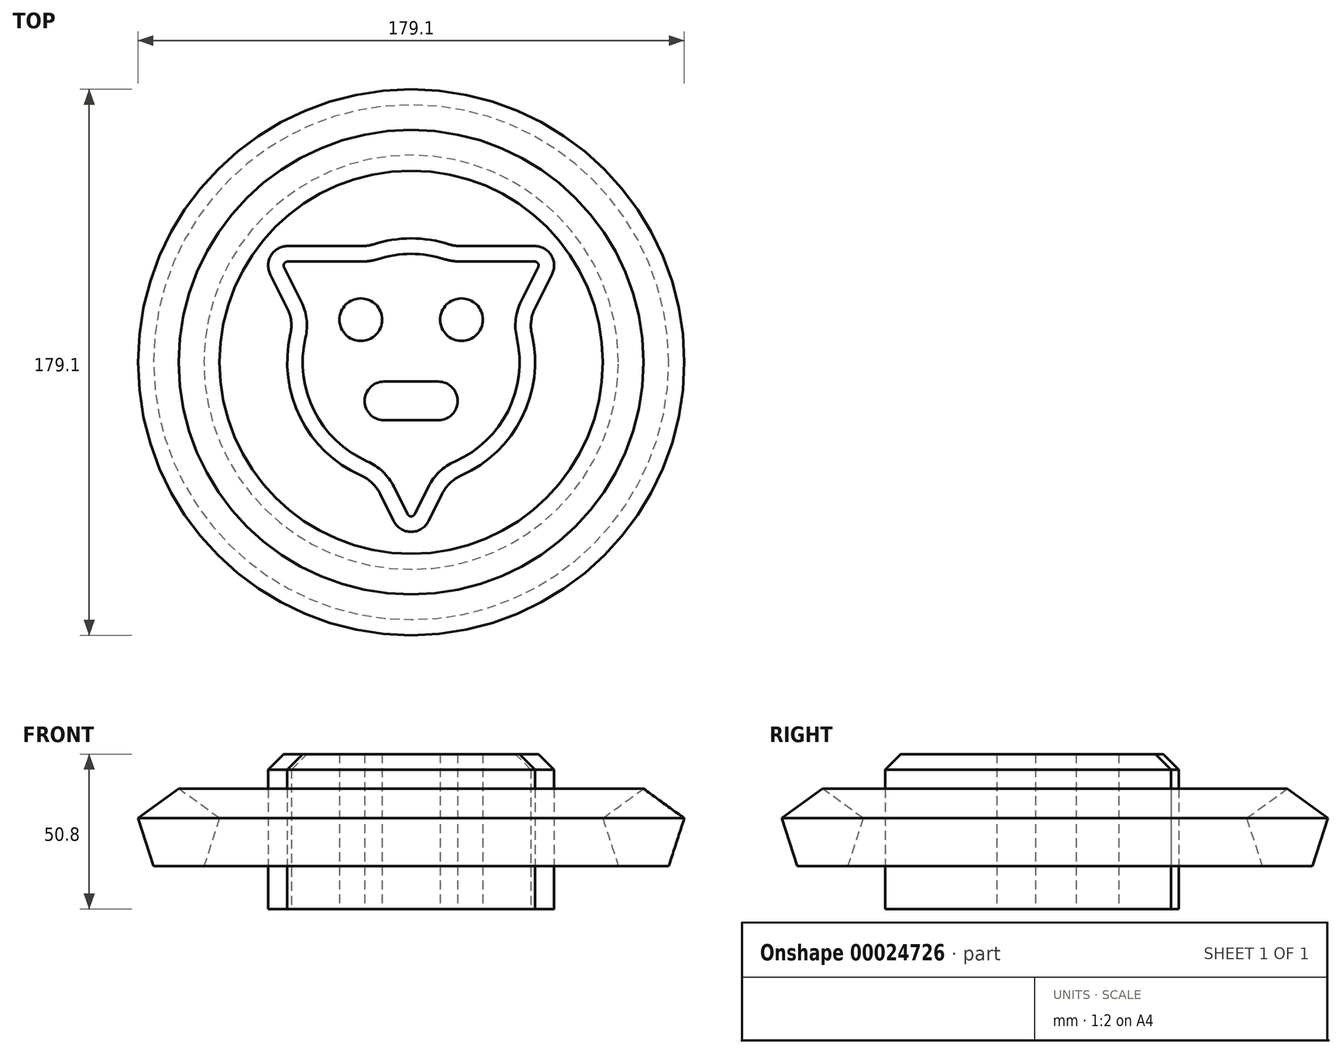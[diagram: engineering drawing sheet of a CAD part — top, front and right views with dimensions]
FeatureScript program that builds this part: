
annotation { "Feature Type Name" : "Feature", "Feature Type Description" : "" }
export const myFeature = defineFeature(function(context is Context, id is Id, definition is map)
    precondition{}
    {
        {
            var Q0;
            Q0=qCreatedBy(makeId("Top.planeOp"),FACE);
            var sketch = newSketch(context, id + "F0", { "sketchPlane" : qUnion([Q0])});
            skArc(sketch, "E0", {"start": v(-38.4, 13.3) * mm, "mid": v(-36.35, -18.17) * mm, "end": v(-12.4, -38.7) * mm});
            skLineSegment(sketch, "E1", {"start": v(-50.8, 38.1) * mm, "end": v(-14.14, 38.1) * mm});
            skLineSegment(sketch, "E2", {"start": v(50.8, 38.1) * mm, "end": v(38.4, 13.3) * mm});
            skLineSegment(sketch, "E3", {"start": v(0, -63.5) * mm, "end": v(-12.4, -38.7) * mm});
            skArc(sketch, "E4.trimOffspring", {"start": v(14.14, 38.1) * mm, "mid": v(0, 40.64) * mm, "end": v(-14.14, 38.1) * mm});
            skArc(sketch, "E5.trimOffspring", {"start": v(12.4, -38.7) * mm, "mid": v(36.35, -18.17) * mm, "end": v(38.4, 13.3) * mm});
            skLineSegment(sketch, "E6.trimOffspring", {"start": v(12.4, -38.7) * mm, "end": v(0, -63.5) * mm});
            skLineSegment(sketch, "E7.trimOffspring", {"start": v(-38.4, 13.3) * mm, "end": v(-50.8, 38.1) * mm});
            skLineSegment(sketch, "E8.trimOffspring", {"start": v(14.14, 38.1) * mm, "end": v(50.8, 38.1) * mm});
            skSolve(sketch);
        }
        {
            var Q0;
            Q0=makeQuery(id+"F0.imprint","IMPRINT",FACE,{"disambiguationData":[TD([[makeQuery(id+"F0.imprint","IMPRINT",EDGE,{"derivedFrom":sQuery(id+"F0.wireOp",EDGE,"E0")}),1.0]])]});
            extrude(context, id + "F1", {"entities" : qUnion([Q0]), "depth" : 50.8 * mm});
        }
        {
            var Q0;
            Q0=makeQuery(id+"F1.opExtrude","SWEPT_EDGE",EDGE,{"disambiguationData":[OSD([sQuery(id+"F0.wireOp",EDGE,"E5.trimOffspring"),sQuery(id+"F0.wireOp",EDGE,"E6.trimOffspring")])]});
            var Q1;
            Q1=makeQuery(id+"F1.opExtrude","SWEPT_EDGE",EDGE,{"disambiguationData":[OSD([sQuery(id+"F0.wireOp",EDGE,"E0"),sQuery(id+"F0.wireOp",EDGE,"E3")])]});
            var Q2;
            Q2=makeQuery(id+"F1.opExtrude","SWEPT_EDGE",EDGE,{"disambiguationData":[OSD([sQuery(id+"F0.wireOp",EDGE,"E0"),sQuery(id+"F0.wireOp",EDGE,"E7.trimOffspring")])]});
            var Q3;
            Q3=makeQuery(id+"F1.opExtrude","SWEPT_EDGE",EDGE,{"disambiguationData":[OSD([sQuery(id+"F0.wireOp",EDGE,"E1"),sQuery(id+"F0.wireOp",EDGE,"E4.trimOffspring")])]});
            var Q4;
            Q4=makeQuery(id+"F1.opExtrude","SWEPT_EDGE",EDGE,{"disambiguationData":[OSD([sQuery(id+"F0.wireOp",EDGE,"E4.trimOffspring"),sQuery(id+"F0.wireOp",EDGE,"E8.trimOffspring")])]});
            var Q5;
            Q5=makeQuery(id+"F1.opExtrude","SWEPT_EDGE",EDGE,{"disambiguationData":[OSD([sQuery(id+"F0.wireOp",EDGE,"E2"),sQuery(id+"F0.wireOp",EDGE,"E5.trimOffspring")])]});
            fillet(context, id + "F2", {"entities" : qUnion([Q0, Q1, Q2, Q3, Q4, Q5]), "radius" : 12.7 * mm, "tangentPropagation" : true, "allowEdgeOverflow" : false});
        }
        {
            var Q0;
            Q0=makeQuery(id+"F1.opExtrude","SWEPT_EDGE",EDGE,{"disambiguationData":[OSD([sQuery(id+"F0.wireOp",EDGE,"E3"),sQuery(id+"F0.wireOp",EDGE,"E6.trimOffspring")])]});
            var Q1;
            Q1=makeQuery(id+"F1.opExtrude","SWEPT_EDGE",EDGE,{"disambiguationData":[OSD([sQuery(id+"F0.wireOp",EDGE,"E2"),sQuery(id+"F0.wireOp",EDGE,"E8.trimOffspring")])]});
            var Q2;
            Q2=makeQuery(id+"F1.opExtrude","SWEPT_EDGE",EDGE,{"disambiguationData":[OSD([sQuery(id+"F0.wireOp",EDGE,"E1"),sQuery(id+"F0.wireOp",EDGE,"E7.trimOffspring")])]});
            fillet(context, id + "F3", {"entities" : qUnion([Q0, Q1, Q2]), "radius" : 6.35 * mm, "tangentPropagation" : true, "allowEdgeOverflow" : false});
        }
        {
            var Q0;
            Q0=makeQuery(id+"F1.opExtrude","CAP_EDGE",EDGE,{"disambiguationData":[OSD([sQuery(id+"F0.wireOp",EDGE,"E0")])],"isStart":false});
            chamfer(context, id + "F4", {"entities" : qUnion([Q0]), "width" : 5.08 * mm, "tangentPropagation" : true});
        }
        {
            var Q0;
            Q0=qCreatedBy(makeId("Top.planeOp"),FACE);
            var sketch = newSketch(context, id + "F5", { "sketchPlane" : qUnion([Q0])});
            skCircle(sketch, "E9", {"center": v(-16.51, 13.97) * mm, "radius": 6.99 * mm});
            skCircle(sketch, "E10", {"center": v(16.51, 13.97) * mm, "radius": 6.99 * mm});
            skArc(sketch, "E11", {"start": v(-8.9, -6.35) * mm, "mid": v(-15.24, -12.7) * mm, "end": v(-8.9, -19.05) * mm});
            skArc(sketch, "E12", {"start": v(8.9, -19.05) * mm, "mid": v(15.24, -12.7) * mm, "end": v(8.9, -6.35) * mm});
            skLineSegment(sketch, "E13", {"start": v(-8.9, -6.35) * mm, "end": v(8.89, -6.35) * mm});
            skLineSegment(sketch, "E14", {"start": v(-8.89, -19.05) * mm, "end": v(8.9, -19.05) * mm});
            skSolve(sketch);
        }
        {
            var Q0;
            Q0 = qSketchRegion(id + "F5", true);
            extrude(context, id + "F6", {"entities" : qUnion([Q0]), "operationType" : NewBodyOperationType.REMOVE, "endBound" : BoundingType.THROUGH_ALL, "depth" : 25.4 * mm});
        }
        {
            var Q0;
            Q0=qCreatedBy(makeId("Front.planeOp"),FACE);
            var sketch = newSketch(context, id + "F7", { "sketchPlane" : qUnion([Q0])});
            skCircle(sketch, "E15.cCircle", {"center": v(-76.2, 25.4) * mm, "radius": 11.36 * mm, "construction": true});
            skLineSegment(sketch, "E15.0", {"start": v(-62.85, 29.74) * mm, "end": v(-67.95, 14.04) * mm});
            skLineSegment(sketch, "E15.1", {"start": v(-67.95, 14.04) * mm, "end": v(-84.45, 14.04) * mm});
            skLineSegment(sketch, "E15.2", {"start": v(-84.45, 14.04) * mm, "end": v(-89.55, 29.74) * mm});
            skLineSegment(sketch, "E15.3", {"start": v(-89.55, 29.74) * mm, "end": v(-76.2, 39.44) * mm});
            skLineSegment(sketch, "E15.4", {"start": v(-76.2, 39.44) * mm, "end": v(-62.85, 29.74) * mm});
            skPoint(sketch, "E15.0.midPoint", {"position": v(-65.4, 21.89) * mm});
            skSolve(sketch);
        }
        {
            var Q0;
            Q0=qCreatedBy(makeId("Front.planeOp"),FACE);
            var sketch = newSketch(context, id + "F8", { "sketchPlane" : qUnion([Q0])});
            skLineSegment(sketch, "E16", {"start": v(0, 72.2) * mm, "end": v(0, -29.85) * mm});
            skSolve(sketch);
        }
        {
            var Q0;
            Q0 = qSketchRegion(id + "F7", true);
            var Q1;
            Q1=sQuery(id+"F8.wireOp",EDGE,"E16");
            revolve(context, id + "F9", {"entities" : qUnion([Q0]), "axis" : qUnion([Q1]), "revolveType" : RevolveType.FULL});
        }
    });
